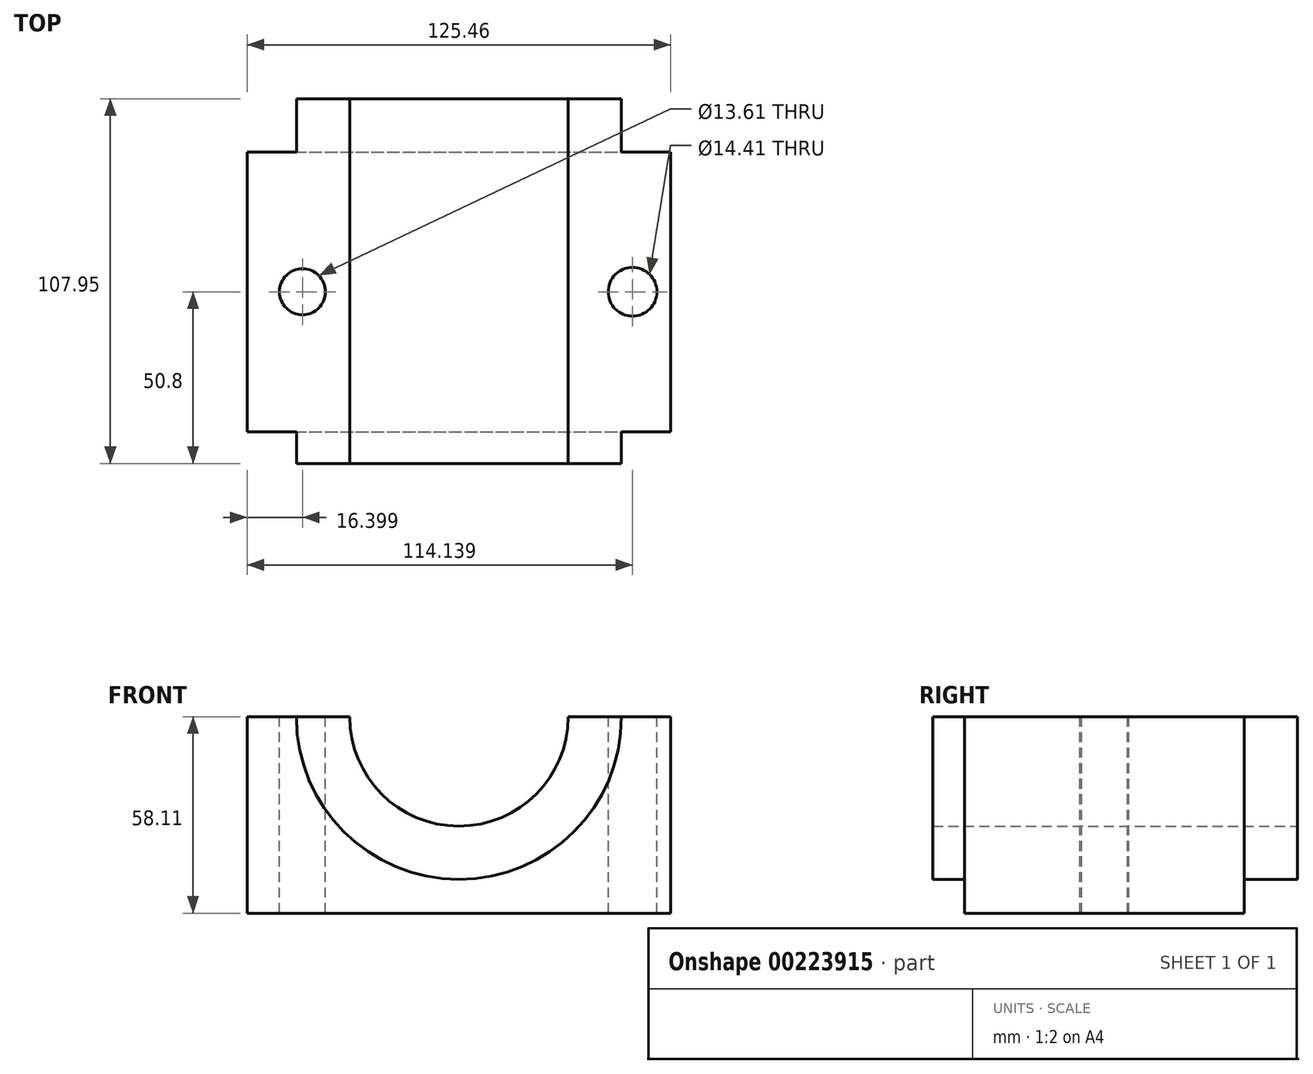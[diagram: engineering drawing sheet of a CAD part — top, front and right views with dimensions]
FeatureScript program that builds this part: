
annotation { "Feature Type Name" : "Feature", "Feature Type Description" : "" }
export const myFeature = defineFeature(function(context is Context, id is Id, definition is map)
    precondition{}
    {
        {
            var Q0;
            Q0=qCreatedBy(makeId("Front.planeOp"),FACE);
            var sketch = newSketch(context, id + "F0", { "sketchPlane" : qUnion([Q0])});
            skLineSegment(sketch, "E0.bottom", {"start": v(-62.73, 58.1) * mm, "end": v(62.73, 58.1) * mm});
            skLineSegment(sketch, "E0.top", {"start": v(-62.73, -58.1) * mm, "end": v(62.73, -58.1) * mm});
            skLineSegment(sketch, "E0.left", {"start": v(-62.73, 58.1) * mm, "end": v(-62.73, -58.1) * mm});
            skLineSegment(sketch, "E0.right", {"start": v(62.73, 58.1) * mm, "end": v(62.73, -58.1) * mm});
            skPoint(sketch, "E0.middle", {"position": v(0, 0) * mm});
            skCircle(sketch, "E1", {"center": v(0, 0) * mm, "radius": 48.13 * mm});
            skCircle(sketch, "E2", {"center": v(0, 0) * mm, "radius": 32.34 * mm});
            skSolve(sketch);
        }
        {
            var Q0;
            Q0=makeQuery(id+"F0.imprint","IMPRINT",FACE,{"disambiguationData":[TD([[makeQuery(id+"F0.imprint","IMPRINT",EDGE,{"derivedFrom":sQuery(id+"F0.wireOp",EDGE,"E1")}),1.0]])]});
            extrude(context, id + "F1", {"entities" : qUnion([Q0]), "depth" : 50.8 * mm});
        }
        {
            var Q0;
            Q0 = qSketchRegion(id + "F0", true);
            extrude(context, id + "F2", {"entities" : qUnion([Q0]), "operationType" : NewBodyOperationType.ADD, "endBound" : BoundingType.SYMMETRIC, "depth" : 82.8 * mm});
        }
        {
            var Q0;
            Q0=makeQuery(id+"F1.opExtrude","CAP_FACE",FACE,{"disambiguationData":[OSD([sQuery(id+"F0.wireOp",EDGE,"E1"),sQuery(id+"F0.wireOp",EDGE,"E2")])],"isStart":true});
            extrude(context, id + "F3", {"entities" : qUnion([Q0]), "operationType" : NewBodyOperationType.ADD, "endBound" : BoundingType.SYMMETRIC, "depth" : 83.82 * mm});
        }
        {
            var Q0;
            Q0=makeQuery(id+"F3.opExtrude","CAP_FACE",FACE,{"disambiguationData":[OSD([sQuery(id+"F0.wireOp",EDGE,"E1"),sQuery(id+"F0.wireOp",EDGE,"E2")])],"isStart":false});
            extrude(context, id + "F4", {"entities" : qUnion([Q0]), "operationType" : NewBodyOperationType.ADD, "endBound" : BoundingType.SYMMETRIC, "depth" : 30.48 * mm});
        }
        {
            var Q0;
            Q0=makeQuery(id+"F2.opExtrude","CAP_FACE",FACE,{"disambiguationData":[OSD([sQuery(id+"F0.wireOp",EDGE,"E0.bottom"),sQuery(id+"F0.wireOp",EDGE,"E0.top"),sQuery(id+"F0.wireOp",EDGE,"E0.left"),sQuery(id+"F0.wireOp",EDGE,"E0.right"),sQuery(id+"F0.wireOp",EDGE,"E1")])],"isStart":true});
            var sketch = newSketch(context, id + "F5", { "sketchPlane" : qUnion([Q0])});
            skLineSegment(sketch, "E3.bottom", {"start": v(-71.82, 0) * mm, "end": v(72.7, 0) * mm});
            skLineSegment(sketch, "E3.top", {"start": v(-71.82, 68.1) * mm, "end": v(72.7, 68.1) * mm});
            skLineSegment(sketch, "E3.left", {"start": v(-71.82, 0) * mm, "end": v(-71.82, 68.1) * mm});
            skLineSegment(sketch, "E3.right", {"start": v(72.7, 0) * mm, "end": v(72.7, 68.1) * mm});
            skSolve(sketch);
        }
        {
            var Q0;
            Q0 = qSketchRegion(id + "F5", true);
            extrude(context, id + "F6", {"entities" : qUnion([Q0]), "operationType" : NewBodyOperationType.ADD, "depth" : 25.4 * mm});
        }
        {
            var Q0;
            Q0=makeQuery(id+"F6.opExtrude","CAP_FACE",FACE,{"disambiguationData":[OSD([sQuery(id+"F5.wireOp",EDGE,"E3.bottom"),sQuery(id+"F5.wireOp",EDGE,"E3.top"),sQuery(id+"F5.wireOp",EDGE,"E3.left"),sQuery(id+"F5.wireOp",EDGE,"E3.right")])],"isStart":false});
            extrude(context, id + "F7", {"entities" : qUnion([Q0]), "operationType" : NewBodyOperationType.REMOVE, "endBound" : BoundingType.THROUGH_ALL, "oppositeDirection" : true, "depth" : 25.4 * mm});
        }
        {
            var Q0;
            {var subQ2=sQuery(id+"F0.wireOp",EDGE,"E0.right");Q0=makeQuery(id+"F7.boolean.opBoolean","COPY",FACE,{"disambiguationData":[TD([makeQuery(id+"F2.opExtrude","SWEPT_FACE",FACE,{"disambiguationData":[OSD([subQ2])]})])],"derivedFrom":makeQuery(id+"F7.opExtrude","SWEPT_FACE",FACE,{"disambiguationData":[OSD([sQuery(id+"F5.wireOp",EDGE,"E3.bottom")])]})});}
            var sketch = newSketch(context, id + "F8", { "sketchPlane" : qUnion([Q0])});
            skCircle(sketch, "E4", {"center": v(51.4, 0) * mm, "radius": 7.2 * mm});
            skCircle(sketch, "E5", {"center": v(-46.33, 0) * mm, "radius": 6.8 * mm});
            skSolve(sketch);
        }
        {
            var Q0;
            Q0=makeQuery(id+"F8.imprint","IMPRINT",FACE,{"disambiguationData":[TD([[makeQuery(id+"F8.imprint","IMPRINT",EDGE,{"derivedFrom":sQuery(id+"F8.wireOp",EDGE,"E5")}),1.0]])]});
            var Q1;
            Q1=makeQuery(id+"F8.imprint","IMPRINT",FACE,{"disambiguationData":[TD([[makeQuery(id+"F8.imprint","IMPRINT",EDGE,{"derivedFrom":sQuery(id+"F8.wireOp",EDGE,"E4")}),1.0]])]});
            extrude(context, id + "F9", {"entities" : qUnion([Q0, Q1]), "operationType" : NewBodyOperationType.REMOVE, "endBound" : BoundingType.THROUGH_ALL, "oppositeDirection" : true, "depth" : 25.4 * mm});
        }
    });
